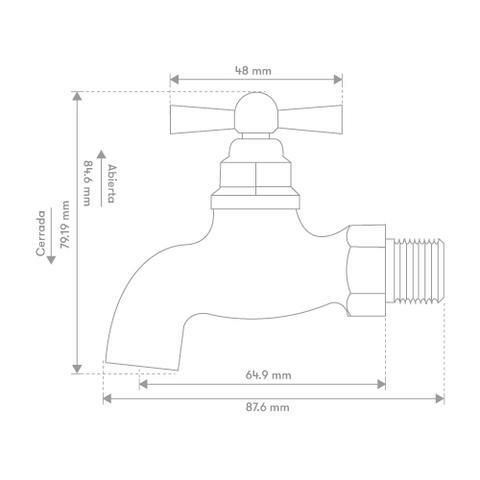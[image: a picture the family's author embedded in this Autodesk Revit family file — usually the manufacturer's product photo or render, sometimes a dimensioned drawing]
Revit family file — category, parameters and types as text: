
# Revit family: 01-9984-13 LLAVE TERMINAL LIVIANA METAL SATINADA
name_source: partatom
category: Aparatos sanitarios
units: mm (PartAtom-declared; Revit-internal decimal feet)

## family parameters
Anfitrión = Cara
Compartido = No
Corte con vacíos al cargar = No
Cota de conector redondo = Diámetro de uso
Número OmniClass = 23.31.11.00
Punto de cálculo de habitación = No
Tipo de pieza = Normal

## types (1)
- 01-9984-13
    Acometida = Dim 1/2" NPT
    Alto = 84.5 mm  [stored 0.277231 ft]
    Ancho = 87.6 mm  [stored 0.287402 ft]
    Ancho manija llave = 48 mm
    Conexión AC = Sí
    Conexión AF = Sí
    Conexión de residuos = No
    Conexión de ventilación = No
    Descripción = Llave jardin
    Elevación por defecto = 0 mm  [stored 0 ft]
    Fabricante = Gricol
    Imagen de tipo = LLAVE TERMINAL LIVIANA METAL SATINADA.jpg
    Link Ficha Tecnica = https://infotecnica.gricol.com
    Metal - Zamak satinado = Metal Zamak Satinado
    Metal Laton Satinado = Metal Laton satinado
    Modelo = 01-9984-13
    Product Name = LLAVE TERMINAL LIVIANA METAL SATINADA
    Salida = Dim 3/4" NH
    URL = https://www.gricol.com

note: [stored X ft] marks values corroborated as IEEE doubles in the binary element streams (Revit-internal decimal feet)

## geometry (parser evidence)
native form markers: Blend x2, Sweep x6
no freeform markers — native parametric forms only
